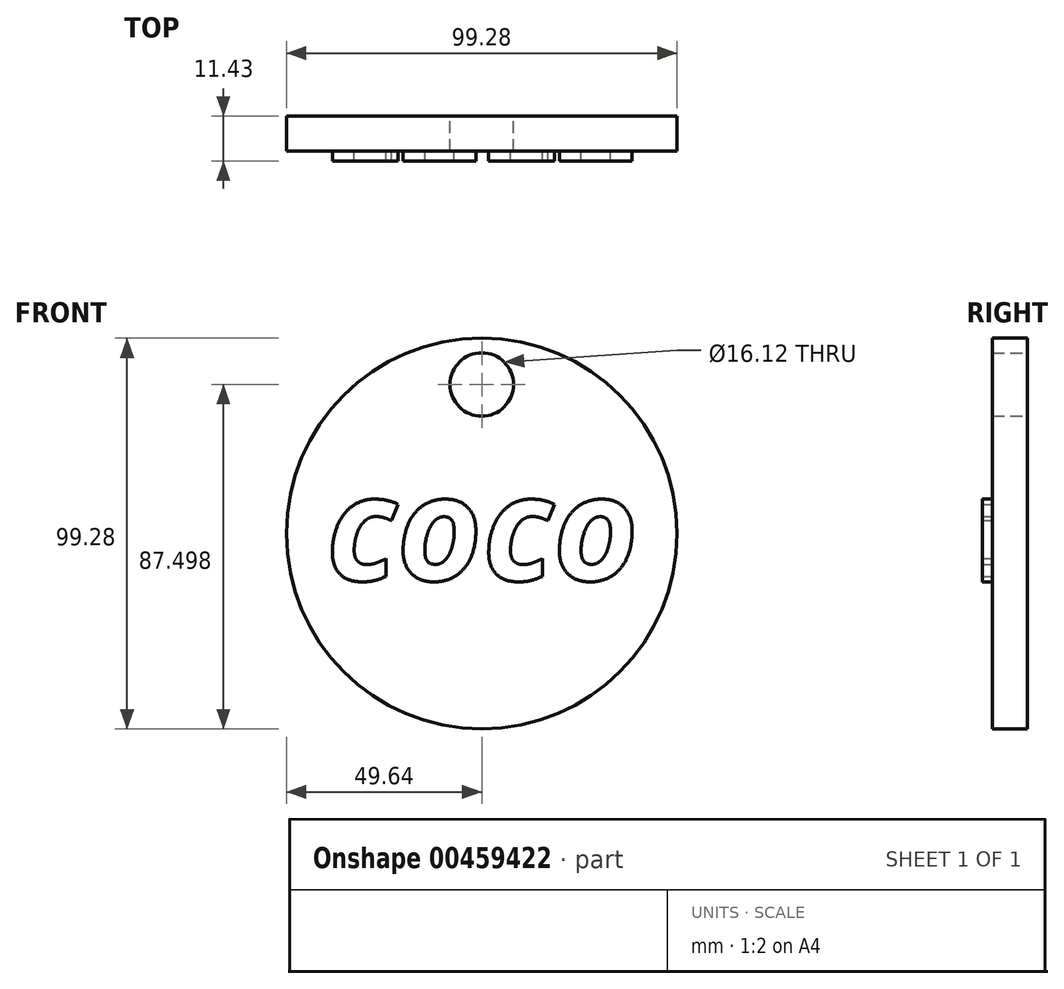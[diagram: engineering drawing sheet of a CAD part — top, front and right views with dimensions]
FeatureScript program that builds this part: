
annotation { "Feature Type Name" : "Feature", "Feature Type Description" : "" }
export const myFeature = defineFeature(function(context is Context, id is Id, definition is map)
    precondition{}
    {
        {
            var Q0;
            Q0=qCreatedBy(makeId("Front.planeOp"),FACE);
            var sketch = newSketch(context, id + "F0", { "sketchPlane" : qUnion([Q0])});
            skCircle(sketch, "E0", {"center": v(0, 0) * mm, "radius": 49.64 * mm});
            skCircle(sketch, "E1", {"center": v(0, 37.86) * mm, "radius": 8.06 * mm});
            skSolve(sketch);
        }
        {
            var Q0;
            Q0=makeQuery(id+"F0.imprint","IMPRINT",FACE,{"disambiguationData":[TD([[makeQuery(id+"F0.imprint","IMPRINT",EDGE,{"derivedFrom":sQuery(id+"F0.wireOp",EDGE,"E0")}),1.0]])]});
            extrude(context, id + "F1", {"entities" : qUnion([Q0]), "depth" : 8.9 * mm});
        }
        {
            var Q0;
            Q0=makeQuery(id+"F1.opExtrude","CAP_FACE",FACE,{"disambiguationData":[OSD([sQuery(id+"F0.wireOp",EDGE,"E0"),sQuery(id+"F0.wireOp",EDGE,"E1")])],"isStart":false});
            var sketch = newSketch(context, id + "F2", { "sketchPlane" : qUnion([Q0])});
            skText(sketch, "E2", { "text": "coco", "fontName": "OpenSans-BoldItalic.ttf"});
            const initialGuessF2  = {"E2": [-0.03957, -0.01193, 1, 0, 0.02677]};
            skSetInitialGuess(sketch, initialGuessF2);
            skSolve(sketch);
        }
        {
            var Q0;
            Q0 = qSketchRegion(id + "F2", true);
            extrude(context, id + "F3", {"entities" : qUnion([Q0]), "operationType" : NewBodyOperationType.ADD, "depth" : 2.54 * mm});
        }
    });
